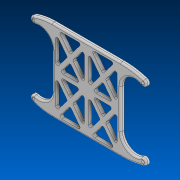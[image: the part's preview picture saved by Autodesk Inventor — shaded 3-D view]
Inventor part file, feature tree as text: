
AUTODESK INVENTOR PART (.ipt)
format: ipt  version: 2022 (Build 260153000, 153)  size: 396,800 bytes
history: native  units: in
note: dims shown in document units (in); Inventor stores cm internally (conversion verified against a paired STEP export)
features: fillet x4, sketch x3, extrude x2, hole x2, mirror x1, projected_geometry x1
ambient origin geometry x8: Origin, YZ Plane, XZ Plane, XY Plane, X Axis, Y Axis, Z Axis, Center Point
bodies: Solid1 (feature_tree)
feature tree (13):
  sketch  "Sketch1"  dims[d0=5.0in d1=6.0in d2=0.25in d3=0.0in]
  extrude  "Extrusion1"  Depth=6.0in
  fillet  "Fillet1"  Radius=0.25in
  hole  "Hole2"  [1 undecoded]
  fillet  "Fillet4"  Radius=0.15in
  extrude  "Extrusion2"  Depth=1.0in
  fillet  "Fillet2"  Radius=0.15in
  fillet  "Fillet3"  Radius=0.15in
  hole  "Hole1"  [1 undecoded]
  mirror  "Mirror1"
  sketch  "Sketch2"  dims[d4=0.25in d5=0.15in d6=0.15in]
  projected_geometry  "Projected Loop1"
  sketch  "Sketch3"  dims[d7=0.15in d8=0.15in d9=0.15in d10=0.15in d11=0.125in d12=1.0in d13=2.3125in d14=0.125in d15=7.0in d16=0.125in d17=0.125in d18=1.0in d19=0.0in d20=0.15in d21=0.05in d22=0.5in d23=0.18in d24=0.75in d25=0.375in d26=0.25in d27=0.5635in d28=1.0in d29=0.8108in d30=0.5in d31=0.175in d32=0.75in d33=0.35in d34=0.2in d35=0.5635in d36=1.0in d37=0.8108in d38=5.0in d39=2.5in d40=0.125in d41=8.0in d42=1.0in]
note: 2 required parameter values undecoded (feature->parameter linkage not recoverable at this tier; creation-order binding heuristic only, values carry confidence <= 0.55)
